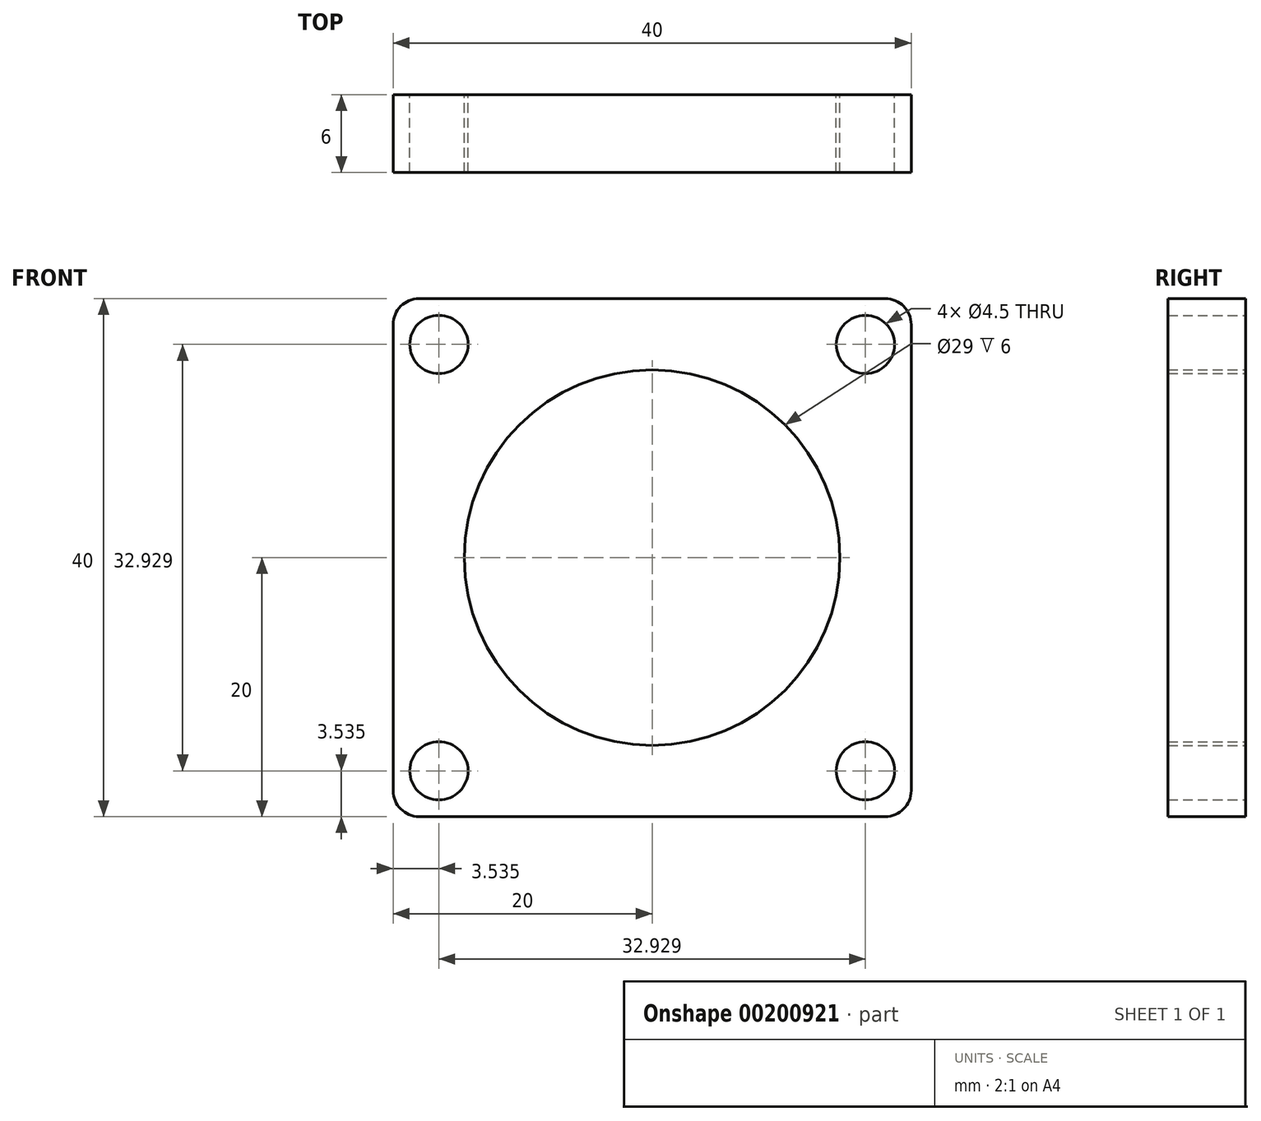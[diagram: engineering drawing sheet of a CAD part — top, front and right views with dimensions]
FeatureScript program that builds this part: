
annotation { "Feature Type Name" : "Feature", "Feature Type Description" : "" }
export const myFeature = defineFeature(function(context is Context, id is Id, definition is map)
    precondition{}
    {
        {
            var Q0;
            Q0=qCreatedBy(makeId("Front.planeOp"),FACE);
            var sketch = newSketch(context, id + "F0", { "sketchPlane" : qUnion([Q0])});
            skLineSegment(sketch, "E0.bottom", {"start": v(-20, 20) * mm, "end": v(20, 20) * mm});
            skLineSegment(sketch, "E0.top", {"start": v(-20, -20) * mm, "end": v(20, -20) * mm});
            skLineSegment(sketch, "E0.left", {"start": v(-20, 20) * mm, "end": v(-20, -20) * mm});
            skLineSegment(sketch, "E0.right", {"start": v(20, 20) * mm, "end": v(20, -20) * mm});
            skCircle(sketch, "E1", {"center": v(0, 0) * mm, "radius": 14.5 * mm});
            skCircle(sketch, "E2", {"center": v(-16.46, 16.46) * mm, "radius": 2.25 * mm});
            skCircle(sketch, "E3", {"center": v(16.46, 16.46) * mm, "radius": 2.25 * mm});
            skCircle(sketch, "E4", {"center": v(16.46, -16.46) * mm, "radius": 2.25 * mm});
            skCircle(sketch, "E5", {"center": v(-16.46, -16.46) * mm, "radius": 2.25 * mm});
            skSolve(sketch);
        }
        {
            var Q0;
            Q0=makeQuery(id+"F0.imprint","IMPRINT",FACE,{"disambiguationData":[TD([[makeQuery(id+"F0.imprint","IMPRINT",EDGE,{"derivedFrom":sQuery(id+"F0.wireOp",EDGE,"E0.bottom")}),-1.0]])]});
            extrude(context, id + "F1", {"entities" : qUnion([Q0]), "depth" : 6 * mm});
        }
        {
            var Q0;
            Q0=makeQuery(id+"F1.opExtrude","SWEPT_EDGE",EDGE,{"disambiguationData":[OSD([sQuery(id+"F0.wireOp",EDGE,"E0.bottom"),sQuery(id+"F0.wireOp",EDGE,"E0.left")])]});
            var Q1;
            Q1=makeQuery(id+"F1.opExtrude","SWEPT_EDGE",EDGE,{"disambiguationData":[OSD([sQuery(id+"F0.wireOp",EDGE,"E0.bottom"),sQuery(id+"F0.wireOp",EDGE,"E0.right")])]});
            var Q2;
            Q2=makeQuery(id+"F1.opExtrude","SWEPT_EDGE",EDGE,{"disambiguationData":[OSD([sQuery(id+"F0.wireOp",EDGE,"E0.top"),sQuery(id+"F0.wireOp",EDGE,"E0.right")])]});
            var Q3;
            Q3=makeQuery(id+"F1.opExtrude","SWEPT_EDGE",EDGE,{"disambiguationData":[OSD([sQuery(id+"F0.wireOp",EDGE,"E0.top"),sQuery(id+"F0.wireOp",EDGE,"E0.left")])]});
            fillet(context, id + "F2", {"entities" : qUnion([Q0, Q1, Q2, Q3]), "radius" : 2 * mm, "tangentPropagation" : true, "allowEdgeOverflow" : false});
        }
    });
